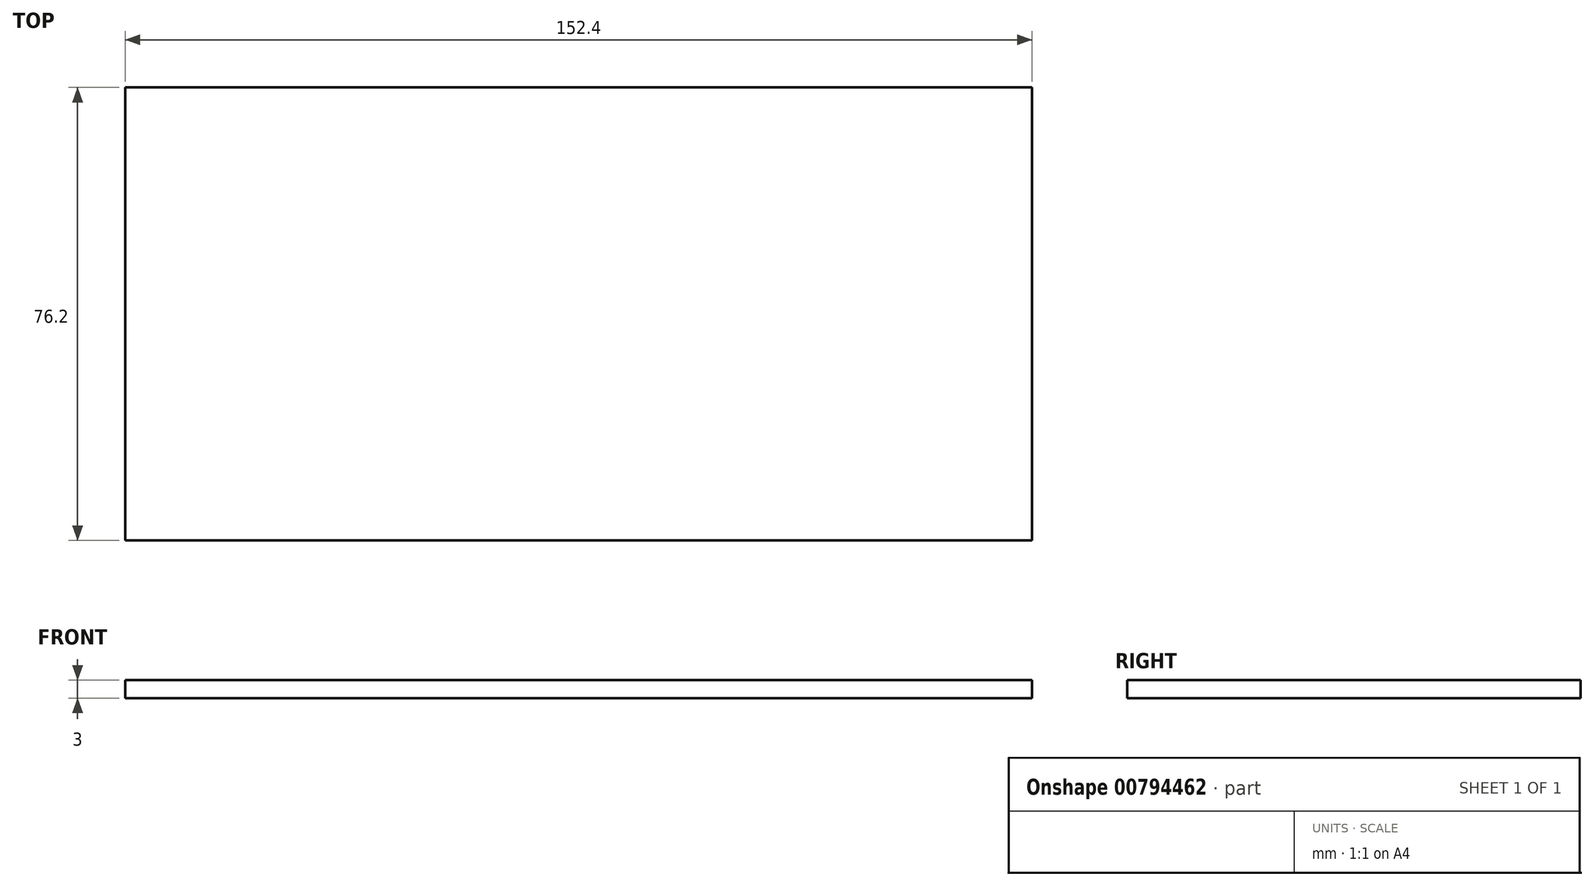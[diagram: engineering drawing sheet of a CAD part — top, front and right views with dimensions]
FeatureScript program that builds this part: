
annotation { "Feature Type Name" : "Feature", "Feature Type Description" : "" }
export const myFeature = defineFeature(function(context is Context, id is Id, definition is map)
    precondition{}
    {
        {
            var Q0;
            Q0=qCreatedBy(makeId("Top.planeOp"),FACE);
            var sketch = newSketch(context, id + "F0", { "sketchPlane" : qUnion([Q0])});
            skLineSegment(sketch, "E0.bottom", {"start": v(0, 0) * mm, "end": v(152.4, 0) * mm});
            skLineSegment(sketch, "E0.top", {"start": v(0, -76.2) * mm, "end": v(152.4, -76.2) * mm});
            skLineSegment(sketch, "E0.left", {"start": v(0, 0) * mm, "end": v(0, -76.2) * mm});
            skLineSegment(sketch, "E0.right", {"start": v(152.4, 0) * mm, "end": v(152.4, -76.2) * mm});
            skSolve(sketch);
        }
        {
            var Q0;
            Q0=makeQuery(id+"F0.imprint","IMPRINT",FACE,{"disambiguationData":[TD([[makeQuery(id+"F0.imprint","IMPRINT",EDGE,{"derivedFrom":sQuery(id+"F0.wireOp",EDGE,"E0.bottom")}),-1.0]])]});
            extrude(context, id + "F1", {"entities" : qUnion([Q0]), "depth" : 3 * mm, "offsetDistance" : 25.4 * mm});
        }
    });
